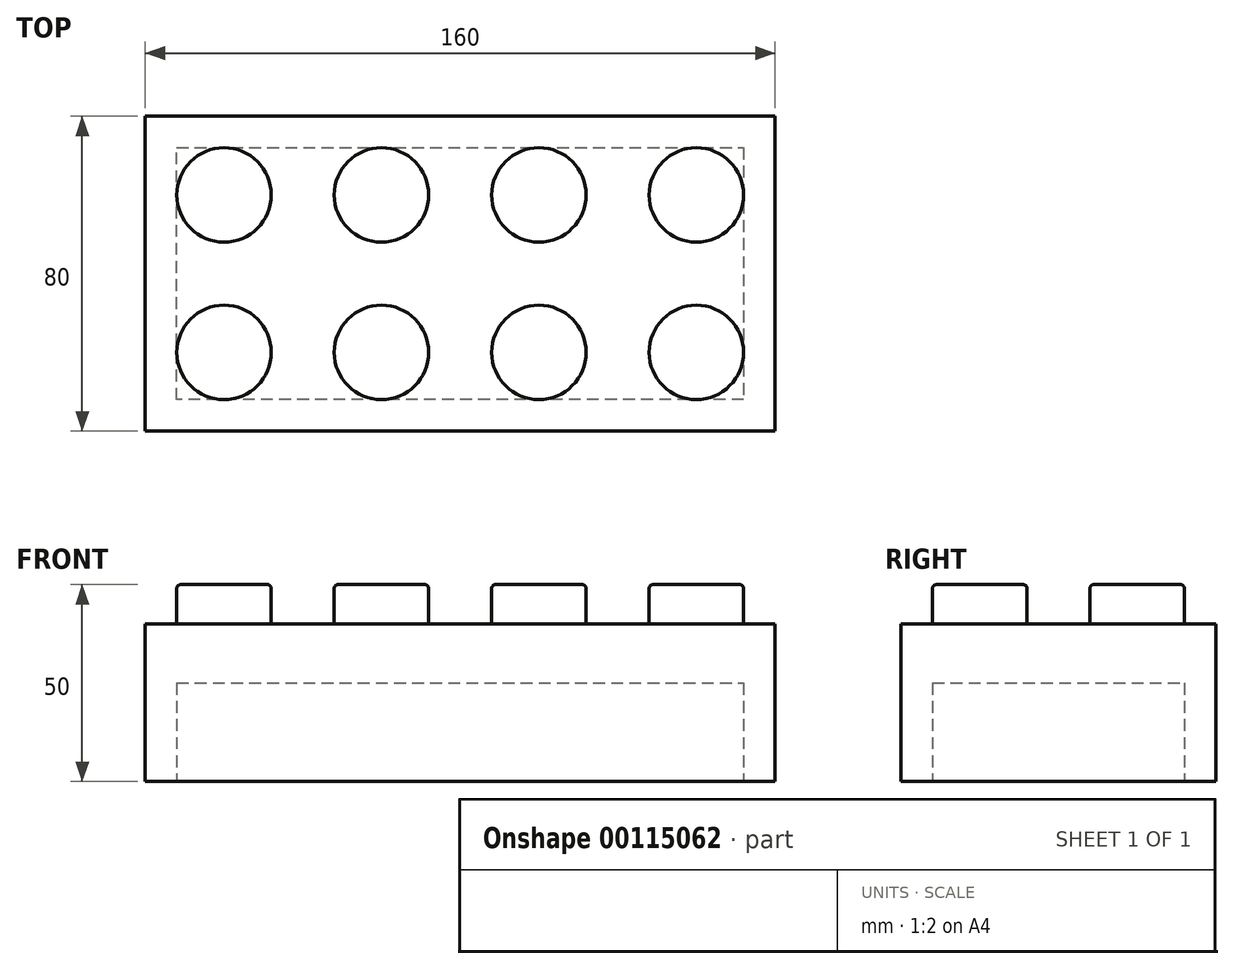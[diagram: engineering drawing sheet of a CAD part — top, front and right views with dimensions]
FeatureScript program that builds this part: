
annotation { "Feature Type Name" : "Feature", "Feature Type Description" : "" }
export const myFeature = defineFeature(function(context is Context, id is Id, definition is map)
    precondition{}
    {
        {
            var Q0;
            Q0=qCreatedBy(makeId("Top.planeOp"),FACE);
            var sketch = newSketch(context, id + "F0", { "sketchPlane" : qUnion([Q0])});
            skLineSegment(sketch, "E0.bottom", {"start": v(-75.01, 26.7) * mm, "end": v(84.99, 26.7) * mm});
            skLineSegment(sketch, "E0.top", {"start": v(-75.01, -53.3) * mm, "end": v(84.99, -53.3) * mm});
            skLineSegment(sketch, "E0.left", {"start": v(-75.01, 26.7) * mm, "end": v(-75.01, -53.3) * mm});
            skLineSegment(sketch, "E0.right", {"start": v(84.99, 26.7) * mm, "end": v(84.99, -53.3) * mm});
            skSolve(sketch);
        }
        {
            var Q0;
            Q0=makeQuery(id+"F0.imprint","IMPRINT",FACE,{"disambiguationData":[TD([[makeQuery(id+"F0.imprint","IMPRINT",EDGE,{"derivedFrom":sQuery(id+"F0.wireOp",EDGE,"E0.bottom")}),-1.0]])]});
            extrude(context, id + "F1", {"entities" : qUnion([Q0]), "depth" : 40 * mm});
        }
        {
            var Q0;
            Q0=makeQuery(id+"F1.opExtrude","CAP_FACE",FACE,{"disambiguationData":[OSD([sQuery(id+"F0.wireOp",EDGE,"E0.bottom"),sQuery(id+"F0.wireOp",EDGE,"E0.top"),sQuery(id+"F0.wireOp",EDGE,"E0.left"),sQuery(id+"F0.wireOp",EDGE,"E0.right")])],"isStart":true});
            var sketch = newSketch(context, id + "F2", { "sketchPlane" : qUnion([Q0])});
            skLineSegment(sketch, "E1.0", {"start": v(-67.01, -18.7) * mm, "end": v(76.99, -18.7) * mm});
            skLineSegment(sketch, "E1.1", {"start": v(-67.01, 45.3) * mm, "end": v(-67.01, -18.7) * mm});
            skLineSegment(sketch, "E1.2", {"start": v(76.99, 45.3) * mm, "end": v(-67.01, 45.3) * mm});
            skLineSegment(sketch, "E1.3", {"start": v(76.99, -18.7) * mm, "end": v(76.99, 45.3) * mm});
            skSolve(sketch);
        }
        {
            var Q0;
            Q0=makeQuery(id+"F2.imprint","IMPRINT",FACE,{"disambiguationData":[TD([[makeQuery(id+"F2.imprint","IMPRINT",EDGE,{"derivedFrom":sQuery(id+"F2.wireOp",EDGE,"E1.0")}),1.0]])]});
            extrude(context, id + "F3", {"entities" : qUnion([Q0]), "operationType" : NewBodyOperationType.REMOVE, "oppositeDirection" : true, "depth" : 25 * mm});
        }
        {
            var Q0;
            Q0=makeQuery(id+"F1.opExtrude","CAP_FACE",FACE,{"disambiguationData":[OSD([sQuery(id+"F0.wireOp",EDGE,"E0.bottom"),sQuery(id+"F0.wireOp",EDGE,"E0.top"),sQuery(id+"F0.wireOp",EDGE,"E0.left"),sQuery(id+"F0.wireOp",EDGE,"E0.right")])],"isStart":false});
            var sketch = newSketch(context, id + "F4", { "sketchPlane" : qUnion([Q0])});
            skCircle(sketch, "E2", {"center": v(-55.01, 6.7) * mm, "radius": 12 * mm});
            skCircle(sketch, "E3.0.1.0", {"center": v(-55.01, -33.3) * mm, "radius": 12 * mm});
            skCircle(sketch, "E3.1.0.0", {"center": v(-15.01, 6.7) * mm, "radius": 12 * mm});
            skCircle(sketch, "E3.1.1.0", {"center": v(-15.01, -33.3) * mm, "radius": 12 * mm});
            skCircle(sketch, "E3.2.0.0", {"center": v(24.99, 6.7) * mm, "radius": 12 * mm});
            skCircle(sketch, "E3.2.1.0", {"center": v(24.99, -33.3) * mm, "radius": 12 * mm});
            skCircle(sketch, "E3.3.0.0", {"center": v(64.99, 6.7) * mm, "radius": 12 * mm});
            skCircle(sketch, "E3.3.1.0", {"center": v(64.99, -33.3) * mm, "radius": 12 * mm});
            skLineSegment(sketch, "E3.direction1", {"start": v(-55.01, 6.7) * mm, "end": v(-15.01, 6.7) * mm, "construction": true});
            skLineSegment(sketch, "E3.direction2", {"start": v(-55.01, 6.7) * mm, "end": v(-55.01, -33.3) * mm, "construction": true});
            skSolve(sketch);
        }
        {
            var Q0;
            Q0 = qSketchRegion(id + "F4", true);
            extrude(context, id + "F5", {"entities" : qUnion([Q0]), "operationType" : NewBodyOperationType.ADD, "depth" : 10 * mm});
        }
        {
            var Q0;
            Q0=makeQuery(id+"F5.opExtrude","CAP_FACE",FACE,{"disambiguationData":[OSD([sQuery(id+"F4.wireOp",EDGE,"E2")])],"isStart":false});
            var Q1;
            Q1=makeQuery(id+"F5.opExtrude","CAP_FACE",FACE,{"disambiguationData":[OSD([sQuery(id+"F4.wireOp",EDGE,"E3.1.0.0")])],"isStart":false});
            var Q2;
            Q2=makeQuery(id+"F5.opExtrude","CAP_FACE",FACE,{"disambiguationData":[OSD([sQuery(id+"F4.wireOp",EDGE,"E3.2.0.0")])],"isStart":false});
            var Q3;
            Q3=makeQuery(id+"F5.opExtrude","CAP_FACE",FACE,{"disambiguationData":[OSD([sQuery(id+"F4.wireOp",EDGE,"E3.3.0.0")])],"isStart":false});
            var Q4;
            Q4=makeQuery(id+"F5.opExtrude","CAP_FACE",FACE,{"disambiguationData":[OSD([sQuery(id+"F4.wireOp",EDGE,"E3.0.1.0")])],"isStart":false});
            var Q5;
            Q5=makeQuery(id+"F5.opExtrude","CAP_EDGE",EDGE,{"disambiguationData":[OSD([sQuery(id+"F4.wireOp",EDGE,"E3.1.1.0")])],"isStart":false});
            var Q6;
            Q6=makeQuery(id+"F5.opExtrude","CAP_FACE",FACE,{"disambiguationData":[OSD([sQuery(id+"F4.wireOp",EDGE,"E3.2.1.0")])],"isStart":false});
            var Q7;
            Q7=makeQuery(id+"F5.opExtrude","CAP_FACE",FACE,{"disambiguationData":[OSD([sQuery(id+"F4.wireOp",EDGE,"E3.3.1.0")])],"isStart":false});
            fillet(context, id + "F6", {"entities" : qUnion([Q0, Q1, Q2, Q3, Q4, Q5, Q6, Q7]), "radius" : 1 * mm, "tangentPropagation" : true, "allowEdgeOverflow" : false});
        }
    });
